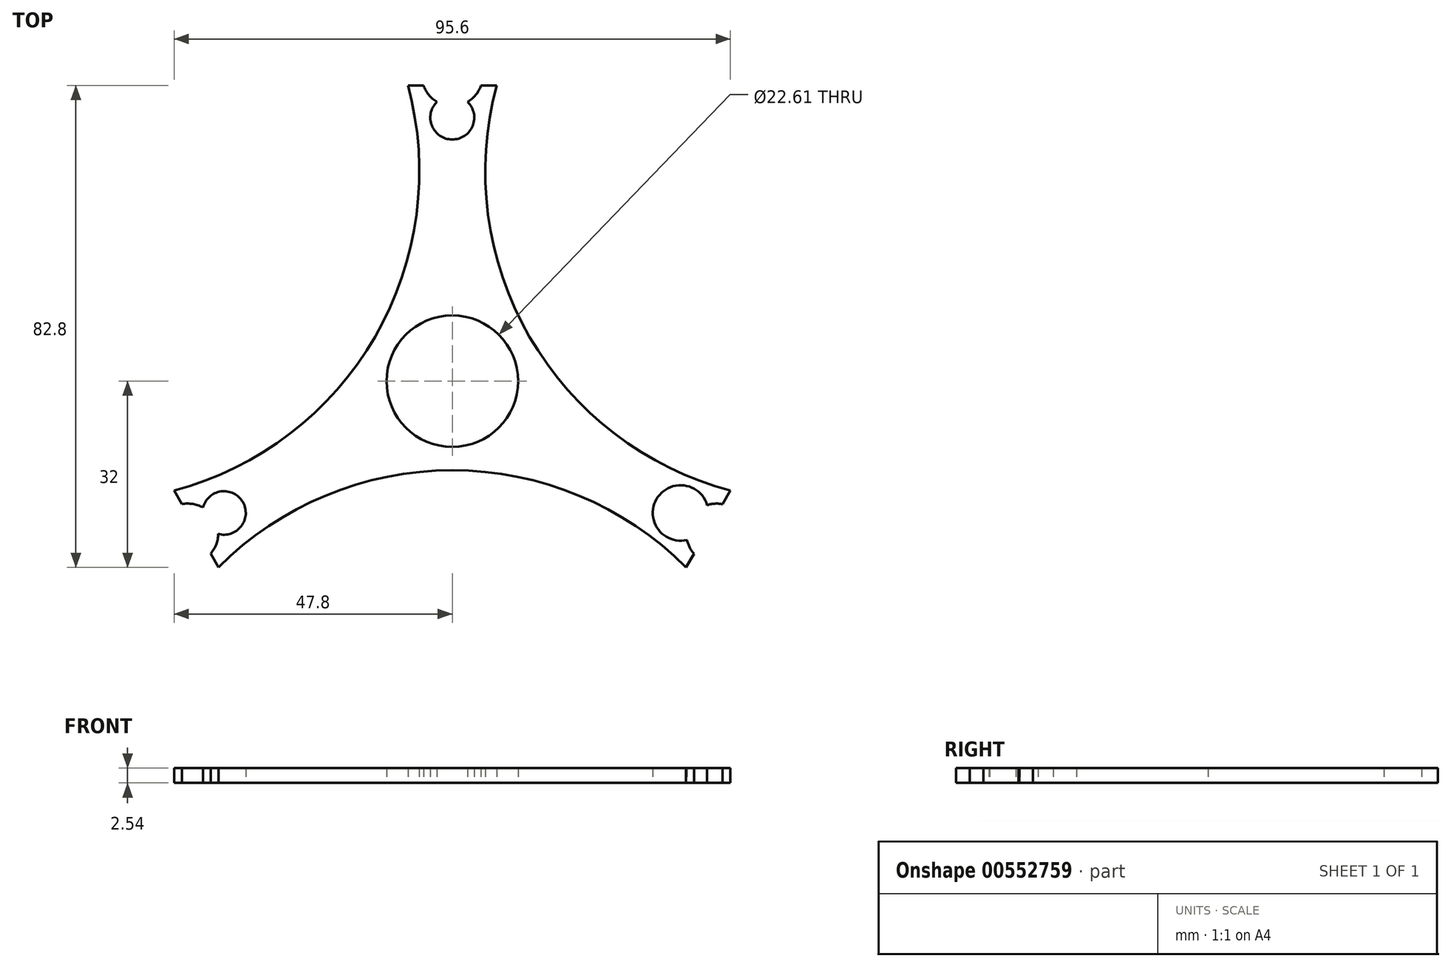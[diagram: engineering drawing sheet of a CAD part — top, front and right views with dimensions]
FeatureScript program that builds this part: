
annotation { "Feature Type Name" : "Feature", "Feature Type Description" : "" }
export const myFeature = defineFeature(function(context is Context, id is Id, definition is map)
    precondition{}
    {
        {
            var Q0;
            Q0=qCreatedBy(makeId("Top.planeOp"),FACE);
            var sketch = newSketch(context, id + "F0", { "sketchPlane" : qUnion([Q0])});
            skCircle(sketch, "E0", {"center": v(0, 0) * mm, "radius": 13.34 * mm});
            skCircle(sketch, "E1.0", {"center": v(0, 0) * mm, "radius": 11.3 * mm});
            skLineSegment(sketch, "E2", {"start": v(0, 0) * mm, "end": v(0, 45.3) * mm});
            skLineSegment(sketch, "E3.1.0", {"start": v(0, 0) * mm, "end": v(-39.23, -22.65) * mm});
            skLineSegment(sketch, "E3.2.0", {"start": v(0, 0) * mm, "end": v(39.23, -22.65) * mm});
            skCircle(sketch, "E4", {"center": v(0, 45.3) * mm, "radius": 3.77 * mm});
            skCircle(sketch, "E5", {"center": v(-39.23, -22.65) * mm, "radius": 3.74 * mm});
            skCircle(sketch, "E6", {"center": v(39.23, -22.65) * mm, "radius": 4.77 * mm});
            skLineSegment(sketch, "E7", {"start": v(-47.8, -18.8) * mm, "end": v(-46.46, -21.14) * mm});
            skLineSegment(sketch, "E8", {"start": v(-40.18, -32) * mm, "end": v(-41.53, -29.66) * mm});
            skArc(sketch, "E9", {"start": v(-41.53, -29.66) * mm, "mid": v(-40.93, -23.63) * mm, "end": v(-46.46, -21.14) * mm});
            skLineSegment(sketch, "E10.1.0", {"start": v(40.18, -32) * mm, "end": v(41.53, -29.66) * mm});
            skArc(sketch, "E10.1.1", {"start": v(46.45, -21.14) * mm, "mid": v(40.93, -23.63) * mm, "end": v(41.53, -29.66) * mm});
            skLineSegment(sketch, "E10.1.2", {"start": v(47.8, -18.8) * mm, "end": v(46.45, -21.14) * mm});
            skLineSegment(sketch, "E10.2.0", {"start": v(7.62, 50.8) * mm, "end": v(4.92, 50.8) * mm});
            skArc(sketch, "E10.2.1", {"start": v(-4.92, 50.8) * mm, "mid": v(0, 47.26) * mm, "end": v(4.92, 50.8) * mm});
            skLineSegment(sketch, "E10.2.2", {"start": v(-7.62, 50.8) * mm, "end": v(-4.92, 50.8) * mm});
            skArc(sketch, "E11", {"start": v(-47.8, -18.8) * mm, "mid": v(-13.26, 7.66) * mm, "end": v(-7.62, 50.8) * mm});
            skArc(sketch, "E12.1.0", {"start": v(40.18, -32) * mm, "mid": v(0, -15.31) * mm, "end": v(-40.18, -32) * mm});
            skArc(sketch, "E12.2.0", {"start": v(7.62, 50.8) * mm, "mid": v(13.26, 7.66) * mm, "end": v(47.8, -18.8) * mm});
            skSolve(sketch);
        }
        {
            var Q0;
            {var subQ14=sQuery(id+"F0.wireOp",EDGE,"E7");Q0=makeQuery(id+"F0.imprint","IMPRINT",FACE,{"disambiguationData":[TD([[makeQuery(id+"F0.imprint","IMPRINT",EDGE,{"derivedFrom":subQ14}),1.0]])]});}
            var Q1;
            {var subQ9=sQuery(id+"F0.wireOp",EDGE,"E10.1.2");Q1=makeQuery(id+"F0.imprint","IMPRINT",FACE,{"disambiguationData":[TD([[makeQuery(id+"F0.imprint","IMPRINT",EDGE,{"derivedFrom":subQ9}),-1.0]])]});}
            var Q2;
            {var subQ0=sQuery(id+"F0.wireOp",EDGE,"E3.1.0");var subQ1=sQuery(id+"F0.wireOp",EDGE,"E0");var subQ2=makeQuery(id+"F0.imprint","INTERSECT",VERTEX,{"derivedFrom":[subQ1,subQ0]});Q2=makeQuery(id+"F0.imprint","IMPRINT",FACE,{"disambiguationData":[TD([[makeQuery(id+"F0.imprint","IMPRINT",EDGE,{"disambiguationData":[TD([[subQ2,-1.0]])],"derivedFrom":subQ1}),1.0]])]});}
            var Q3;
            {var subQ10=sQuery(id+"F0.wireOp",EDGE,"E8");Q3=makeQuery(id+"F0.imprint","IMPRINT",FACE,{"disambiguationData":[TD([[makeQuery(id+"F0.imprint","IMPRINT",EDGE,{"derivedFrom":subQ10}),-1.0]])]});}
            var Q4;
            {var subQ0=sQuery(id+"F0.wireOp",EDGE,"E2");var subQ1=sQuery(id+"F0.wireOp",EDGE,"E0");var subQ2=makeQuery(id+"F0.imprint","INTERSECT",VERTEX,{"derivedFrom":[subQ1,subQ0]});Q4=makeQuery(id+"F0.imprint","IMPRINT",FACE,{"disambiguationData":[TD([[makeQuery(id+"F0.imprint","IMPRINT",EDGE,{"disambiguationData":[TD([[subQ2,1.0]])],"derivedFrom":subQ1}),1.0]])]});}
            var Q5;
            {var subQ0=sQuery(id+"F0.wireOp",EDGE,"E3.1.0");var subQ1=sQuery(id+"F0.wireOp",EDGE,"E0");var subQ2=makeQuery(id+"F0.imprint","INTERSECT",VERTEX,{"derivedFrom":[subQ1,subQ0]});Q5=makeQuery(id+"F0.imprint","IMPRINT",FACE,{"disambiguationData":[TD([[makeQuery(id+"F0.imprint","IMPRINT",EDGE,{"disambiguationData":[TD([[subQ2,1.0]])],"derivedFrom":subQ1}),1.0]])]});}
            extrude(context, id + "F1", {"entities" : qUnion([Q0, Q1, Q2, Q3, Q4, Q5]), "depth" : 2.54 * mm, "offsetDistance" : 25.4 * mm});
        }
    });
